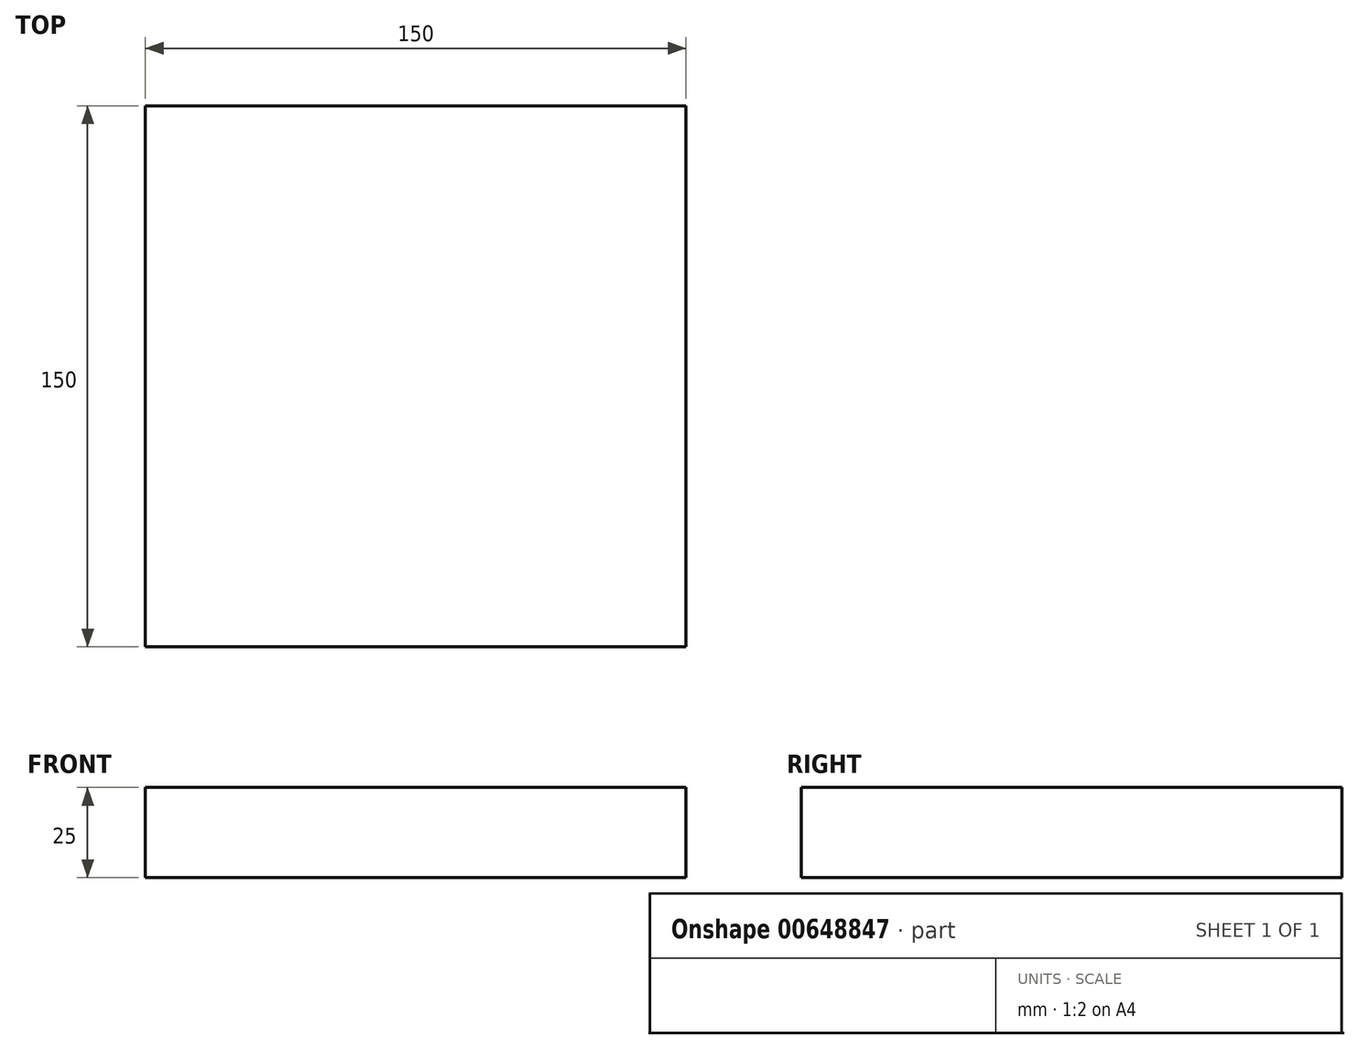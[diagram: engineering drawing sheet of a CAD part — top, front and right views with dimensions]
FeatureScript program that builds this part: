
annotation { "Feature Type Name" : "Feature", "Feature Type Description" : "" }
export const myFeature = defineFeature(function(context is Context, id is Id, definition is map)
    precondition{}
    {
        {
            var Q0;
            Q0=qCreatedBy(makeId("Top.planeOp"),FACE);
            var sketch = newSketch(context, id + "F0", { "sketchPlane" : qUnion([Q0])});
            skLineSegment(sketch, "E0.bottom", {"start": v(75, 75) * mm, "end": v(-75, 75) * mm});
            skLineSegment(sketch, "E0.top", {"start": v(75, -75) * mm, "end": v(-75, -75) * mm});
            skLineSegment(sketch, "E0.left", {"start": v(75, 75) * mm, "end": v(75, -75) * mm});
            skLineSegment(sketch, "E0.right", {"start": v(-75, 75) * mm, "end": v(-75, -75) * mm});
            skPoint(sketch, "E0.middle", {"position": v(0, 0) * mm});
            skSolve(sketch);
        }
        {
            var Q0;
            Q0 = qSketchRegion(id + "F0", true);
            extrude(context, id + "F1", {"entities" : qUnion([Q0]), "depth" : 25 * mm, "offsetDistance" : 25 * mm});
        }
    });
